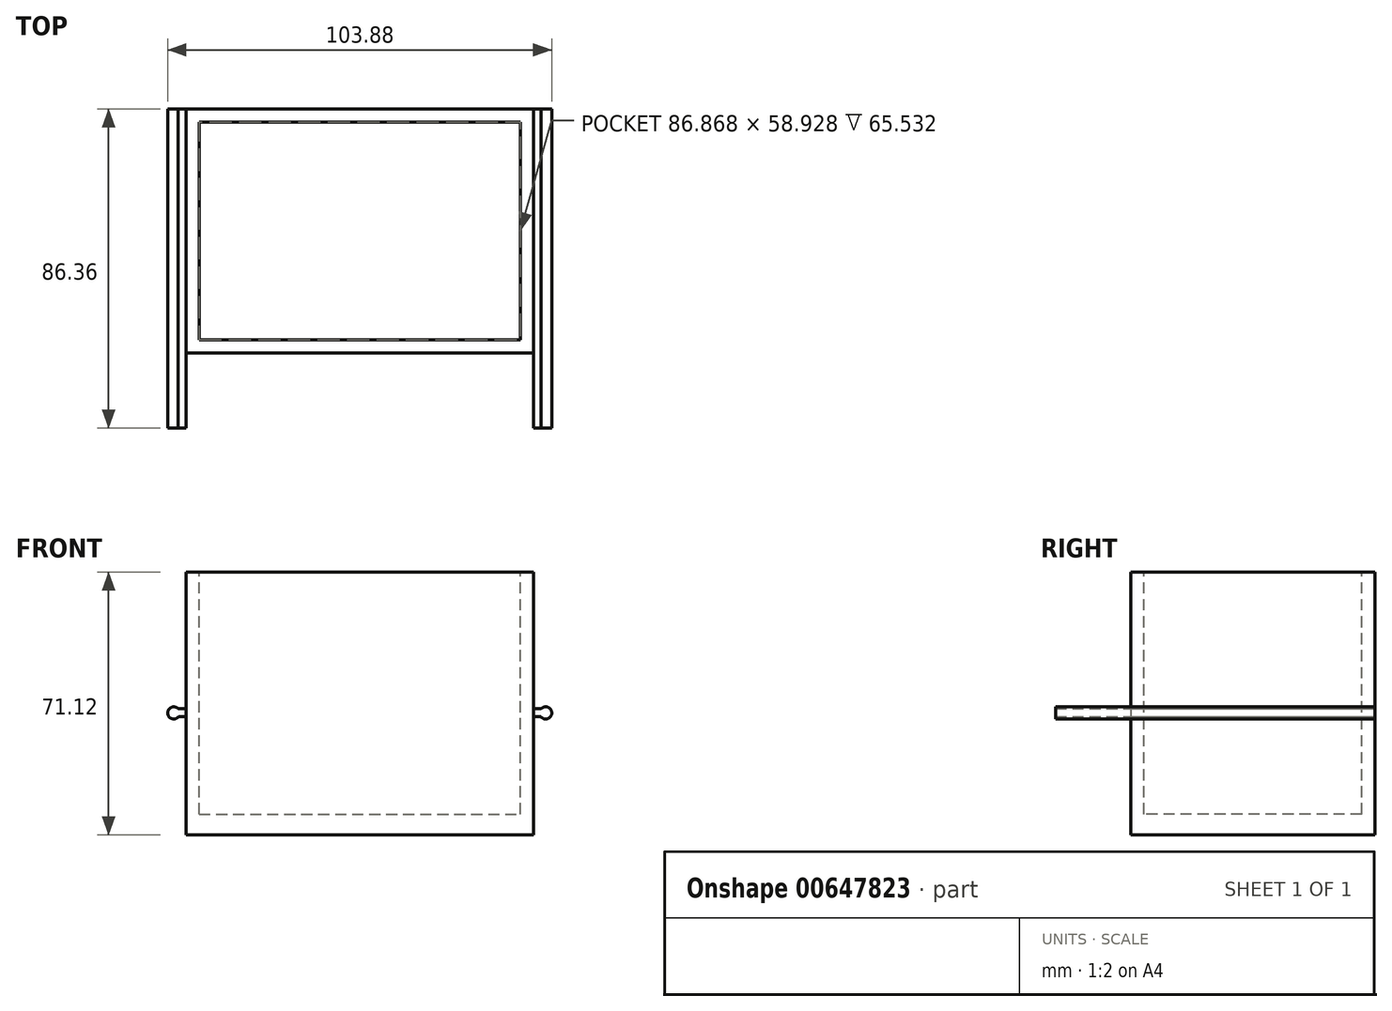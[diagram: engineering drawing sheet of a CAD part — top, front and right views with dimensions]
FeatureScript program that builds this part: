
annotation { "Feature Type Name" : "Feature", "Feature Type Description" : "" }
export const myFeature = defineFeature(function(context is Context, id is Id, definition is map)
    precondition{}
    {
        {
            var Q0;
            Q0=qCreatedBy(makeId("Top.planeOp"),FACE);
            var sketch = newSketch(context, id + "F0", { "sketchPlane" : qUnion([Q0])});
            skLineSegment(sketch, "E0.bottom", {"start": v(-47, -33.02) * mm, "end": v(47, -33.02) * mm});
            skLineSegment(sketch, "E0.top", {"start": v(-47, 33.02) * mm, "end": v(47, 33.02) * mm});
            skLineSegment(sketch, "E0.left", {"start": v(-47, -33.02) * mm, "end": v(-47, 33.02) * mm});
            skLineSegment(sketch, "E0.right", {"start": v(47, -33.02) * mm, "end": v(47, 33.02) * mm});
            skLineSegment(sketch, "E1", {"start": v(0, -33.02) * mm, "end": v(0, 0) * mm});
            skLineSegment(sketch, "E2", {"start": v(-47, 0) * mm, "end": v(0, 0) * mm});
            skSolve(sketch);
        }
        {
            var Q0;
            Q0=makeQuery(id+"F0.imprint","IMPRINT",FACE,{"disambiguationData":[TD([[makeQuery(id+"F0.imprint","IMPRINT",EDGE,{"derivedFrom":sQuery(id+"F0.wireOp",EDGE,"E0.bottom")}),1.0]])]});
            var Q1;
            {var subQ2=sQuery(id+"F0.wireOp",EDGE,"E0.top");Q1=makeQuery(id+"F0.imprint","IMPRINT",FACE,{"disambiguationData":[TD([[makeQuery(id+"F0.imprint","IMPRINT",EDGE,{"derivedFrom":subQ2}),-1.0]])]});}
            extrude(context, id + "F1", {"entities" : qUnion([Q0, Q1]), "depth" : 71.12 * mm, "offsetDistance" : 25.4 * mm});
        }
        {
            var Q0;
            Q0=makeQuery(id+"F1.opExtrude","SWEPT_FACE",FACE,{"disambiguationData":[OSD([sQuery(id+"F0.wireOp",EDGE,"E0.top")])]});
            var sketch = newSketch(context, id + "F2", { "sketchPlane" : qUnion([Q0])});
            skCircle(sketch, "E3", {"center": v(50.3, 33.02) * mm, "radius": 1.65 * mm});
            skLineSegment(sketch, "E4", {"start": v(0, 0) * mm, "end": v(0, 71.12) * mm});
            skCircle(sketch, "E5.MirrorC", {"center": v(-50.3, 33.02) * mm, "radius": 1.65 * mm});
            skLineSegment(sketch, "E6.bottom", {"start": v(49.1, 34.16) * mm, "end": v(44.73, 34.16) * mm});
            skLineSegment(sketch, "E6.top", {"start": v(49.1, 31.98) * mm, "end": v(44.73, 31.98) * mm});
            skLineSegment(sketch, "E6.left", {"start": v(49.1, 34.16) * mm, "end": v(49.1, 31.98) * mm});
            skLineSegment(sketch, "E6.right", {"start": v(44.73, 34.16) * mm, "end": v(44.73, 31.98) * mm});
            skSolve(sketch);
        }
        {
            var Q0;
            {var subQ1=sQuery(id+"F2.wireOp",EDGE,"E3");var subQ3=sQuery(id+"F2.wireOp",EDGE,"E6.top");var subQ4=makeQuery(id+"F2.imprint","INTERSECT",VERTEX,{"derivedFrom":[subQ1,subQ3]});Q0=makeQuery(id+"F2.imprint","IMPRINT",FACE,{"disambiguationData":[TD([[makeQuery(id+"F2.imprint","IMPRINT",EDGE,{"disambiguationData":[TD([[subQ4,1.0]])],"derivedFrom":subQ1}),-1.0]])]});}
            var Q1;
            {var subQ0=sQuery(id+"F2.wireOp",EDGE,"E6.left");Q1=makeQuery(id+"F2.imprint","IMPRINT",FACE,{"disambiguationData":[TD([[makeQuery(id+"F2.imprint","IMPRINT",EDGE,{"derivedFrom":subQ0}),-1.0]])]});}
            var Q2;
            {var subQ0=sQuery(id+"F2.wireOp",EDGE,"E6.left");Q2=makeQuery(id+"F2.imprint","IMPRINT",FACE,{"disambiguationData":[TD([[makeQuery(id+"F2.imprint","IMPRINT",EDGE,{"derivedFrom":subQ0}),1.0]])]});}
            extrude(context, id + "F3", {"entities" : qUnion([Q0, Q1, Q2]), "oppositeDirection" : true, "depth" : 86.36 * mm, "offsetDistance" : 25.4 * mm});
        }
        {
            var Q0;
            Q0=makeQuery(id+"F3.opExtrude","SWEPT_BODY",BODY,{"disambiguationData":[OSD([sQuery(id+"F0.wireOp",EDGE,"E0.top"),sQuery(id+"F0.wireOp",EDGE,"E0.left"),sQuery(id+"F2.wireOp",EDGE,"E3"),sQuery(id+"F2.wireOp",EDGE,"E6.bottom"),sQuery(id+"F2.wireOp",EDGE,"E6.top")])]});
            var Q1;
            Q1=qCreatedBy(makeId("Right.planeOp"),FACE);
            mirror(context, id + "F4", {"operationType" : NewBodyOperationType.ADD, "entities" : qUnion([Q0]), "mirrorPlane" : qUnion([Q1])});
        }
        {
            var Q0;
            Q0=makeQuery(id+"F1.opExtrude","CAP_FACE",FACE,{"disambiguationData":[OSD([sQuery(id+"F0.wireOp",EDGE,"E0.bottom"),sQuery(id+"F0.wireOp",EDGE,"E0.top"),sQuery(id+"F0.wireOp",EDGE,"E0.left"),sQuery(id+"F0.wireOp",EDGE,"E0.right")])],"isStart":false});
            var sketch = newSketch(context, id + "F5", { "sketchPlane" : qUnion([Q0])});
            skLineSegment(sketch, "E7.bottom", {"start": v(-43.43, 29.46) * mm, "end": v(43.43, 29.46) * mm});
            skLineSegment(sketch, "E7.top", {"start": v(-43.43, -29.46) * mm, "end": v(43.43, -29.46) * mm});
            skLineSegment(sketch, "E7.left", {"start": v(-43.43, 29.46) * mm, "end": v(-43.43, -29.46) * mm});
            skLineSegment(sketch, "E7.right", {"start": v(43.43, 29.46) * mm, "end": v(43.43, -29.46) * mm});
            skPoint(sketch, "E7.middle", {"position": v(0, 0) * mm});
            skSolve(sketch);
        }
        {
            var Q0;
            Q0=makeQuery(id+"F5.imprint","IMPRINT",FACE,{"disambiguationData":[TD([[makeQuery(id+"F5.imprint","IMPRINT",EDGE,{"derivedFrom":sQuery(id+"F5.wireOp",EDGE,"E7.bottom")}),-1.0]])]});
            extrude(context, id + "F6", {"entities" : qUnion([Q0]), "operationType" : NewBodyOperationType.REMOVE, "oppositeDirection" : true, "depth" : 65.53 * mm, "offsetDistance" : 25.4 * mm});
        }
    });
